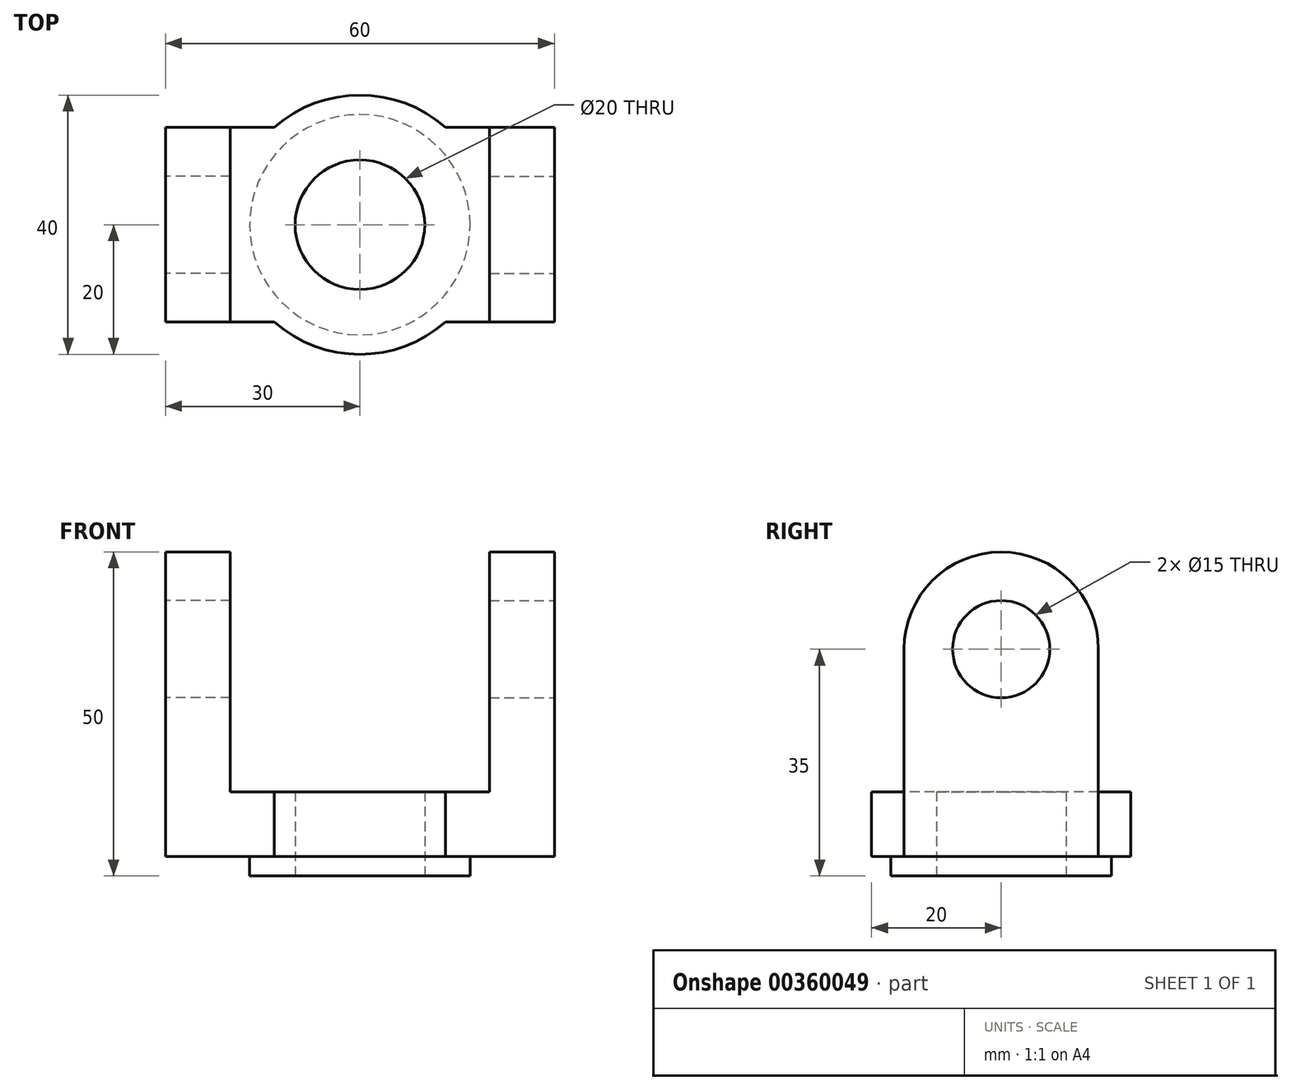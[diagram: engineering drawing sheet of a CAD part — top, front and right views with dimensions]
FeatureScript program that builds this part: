
annotation { "Feature Type Name" : "Feature", "Feature Type Description" : "" }
export const myFeature = defineFeature(function(context is Context, id is Id, definition is map)
    precondition{}
    {
        {
            var Q0;
            Q0=qCreatedBy(makeId("Top.planeOp"),FACE);
            var sketch = newSketch(context, id + "F0", { "sketchPlane" : qUnion([Q0])});
            skLineSegment(sketch, "E0.bottom", {"start": v(0, 0) * mm, "end": v(-16.77, 0) * mm});
            skLineSegment(sketch, "E0.top", {"start": v(0, -30) * mm, "end": v(-16.77, -30) * mm});
            skLineSegment(sketch, "E0.left", {"start": v(0, 0) * mm, "end": v(0, -30) * mm});
            skLineSegment(sketch, "E0.right", {"start": v(-60, 0) * mm, "end": v(-60, -30) * mm});
            skArc(sketch, "E1", {"start": v(-43.23, -30) * mm, "mid": v(-30, -35) * mm, "end": v(-16.77, -30) * mm});
            skPoint(sketch, "E1.centerSnap0", {"position": v(0, -15) * mm});
            skCircle(sketch, "E2", {"center": v(-30, -15) * mm, "radius": 10 * mm});
            skArc(sketch, "E3.trimOffspring", {"start": v(-16.77, 0) * mm, "mid": v(-30, 5) * mm, "end": v(-43.23, 0) * mm});
            skLineSegment(sketch, "E4.trimOffspring", {"start": v(-43.23, -30) * mm, "end": v(-60, -30) * mm});
            skLineSegment(sketch, "E5.trimOffspring", {"start": v(-43.23, 0) * mm, "end": v(-60, 0) * mm});
            skSolve(sketch);
        }
        {
            var Q0;
            Q0=makeQuery(id+"F0.imprint","IMPRINT",FACE,{"disambiguationData":[TD([[makeQuery(id+"F0.imprint","IMPRINT",EDGE,{"derivedFrom":sQuery(id+"F0.wireOp",EDGE,"E0.bottom")}),1.0]])]});
            extrude(context, id + "F1", {"entities" : qUnion([Q0]), "depth" : 10 * mm});
        }
        {
            var Q0;
            Q0=makeQuery(id+"F1.opExtrude","CAP_FACE",FACE,{"disambiguationData":[OSD([sQuery(id+"F0.wireOp",EDGE,"E0.bottom"),sQuery(id+"F0.wireOp",EDGE,"E0.top"),sQuery(id+"F0.wireOp",EDGE,"E0.left"),sQuery(id+"F0.wireOp",EDGE,"E0.right"),sQuery(id+"F0.wireOp",EDGE,"E1"),sQuery(id+"F0.wireOp",EDGE,"E2"),sQuery(id+"F0.wireOp",EDGE,"E3.trimOffspring"),sQuery(id+"F0.wireOp",EDGE,"E4.trimOffspring"),sQuery(id+"F0.wireOp",EDGE,"E5.trimOffspring")])],"isStart":true});
            var sketch = newSketch(context, id + "F2", { "sketchPlane" : qUnion([Q0])});
            skCircle(sketch, "E6", {"center": v(-30, 15) * mm, "radius": 17 * mm});
            skSolve(sketch);
        }
        {
            var Q0;
            Q0=makeQuery(id+"F2.imprint","IMPRINT",FACE,{"disambiguationData":[TD([[makeQuery(id+"F2.imprint","IMPRINT",EDGE,{"derivedFrom":sQuery(id+"F2.wireOp",EDGE,"E6")}),1.0]])]});
            extrude(context, id + "F3", {"entities" : qUnion([Q0]), "operationType" : NewBodyOperationType.ADD, "depth" : 3 * mm});
        }
        {
            var Q0;
            Q0=makeQuery(id+"F1.opExtrude","SWEPT_FACE",FACE,{"disambiguationData":[OSD([sQuery(id+"F0.wireOp",EDGE,"E0.left")])]});
            var sketch = newSketch(context, id + "F4", { "sketchPlane" : qUnion([Q0])});
            skCircle(sketch, "E7", {"center": v(-15, 32) * mm, "radius": 7.5 * mm});
            skPoint(sketch, "E7.centerSnap0", {"position": v(-15, 10) * mm});
            skArc(sketch, "E8", {"start": v(-30, 32) * mm, "mid": v(-15, 47) * mm, "end": v(0, 32) * mm});
            skLineSegment(sketch, "E9", {"start": v(-30, 32) * mm, "end": v(-30, 10) * mm});
            skLineSegment(sketch, "E10", {"start": v(-30, 10) * mm, "end": v(0, 10) * mm});
            skLineSegment(sketch, "E11", {"start": v(0, 10) * mm, "end": v(0, 32) * mm});
            skSolve(sketch);
        }
        {
            var Q0;
            Q0=makeQuery(id+"F4.imprint","IMPRINT",FACE,{"disambiguationData":[TD([[makeQuery(id+"F4.imprint","IMPRINT",EDGE,{"derivedFrom":sQuery(id+"F4.wireOp",EDGE,"E7")}),-1.0]])]});
            extrude(context, id + "F5", {"entities" : qUnion([Q0]), "operationType" : NewBodyOperationType.ADD, "oppositeDirection" : true, "depth" : 10 * mm});
        }
        {
            var Q0;
            Q0=makeQuery(id+"F1.opExtrude","SWEPT_FACE",FACE,{"disambiguationData":[OSD([sQuery(id+"F0.wireOp",EDGE,"E0.right")])]});
            var sketch = newSketch(context, id + "F6", { "sketchPlane" : qUnion([Q0])});
            skCircle(sketch, "E12", {"center": v(15, 32) * mm, "radius": 7.5 * mm});
            skPoint(sketch, "E12.centerSnap0", {"position": v(15, 10) * mm});
            skArc(sketch, "E13", {"start": v(0, 32) * mm, "mid": v(15, 47) * mm, "end": v(30, 32) * mm});
            skLineSegment(sketch, "E14", {"start": v(0, 32) * mm, "end": v(0, 10) * mm});
            skLineSegment(sketch, "E15", {"start": v(0, 10) * mm, "end": v(30, 10) * mm});
            skLineSegment(sketch, "E16", {"start": v(30, 10) * mm, "end": v(30, 32) * mm});
            skSolve(sketch);
        }
        {
            var Q0;
            Q0=makeQuery(id+"F6.imprint","IMPRINT",FACE,{"disambiguationData":[TD([[makeQuery(id+"F6.imprint","IMPRINT",EDGE,{"derivedFrom":sQuery(id+"F6.wireOp",EDGE,"E12")}),-1.0]])]});
            extrude(context, id + "F7", {"entities" : qUnion([Q0]), "operationType" : NewBodyOperationType.ADD, "oppositeDirection" : true, "depth" : 10 * mm});
        }
    });
